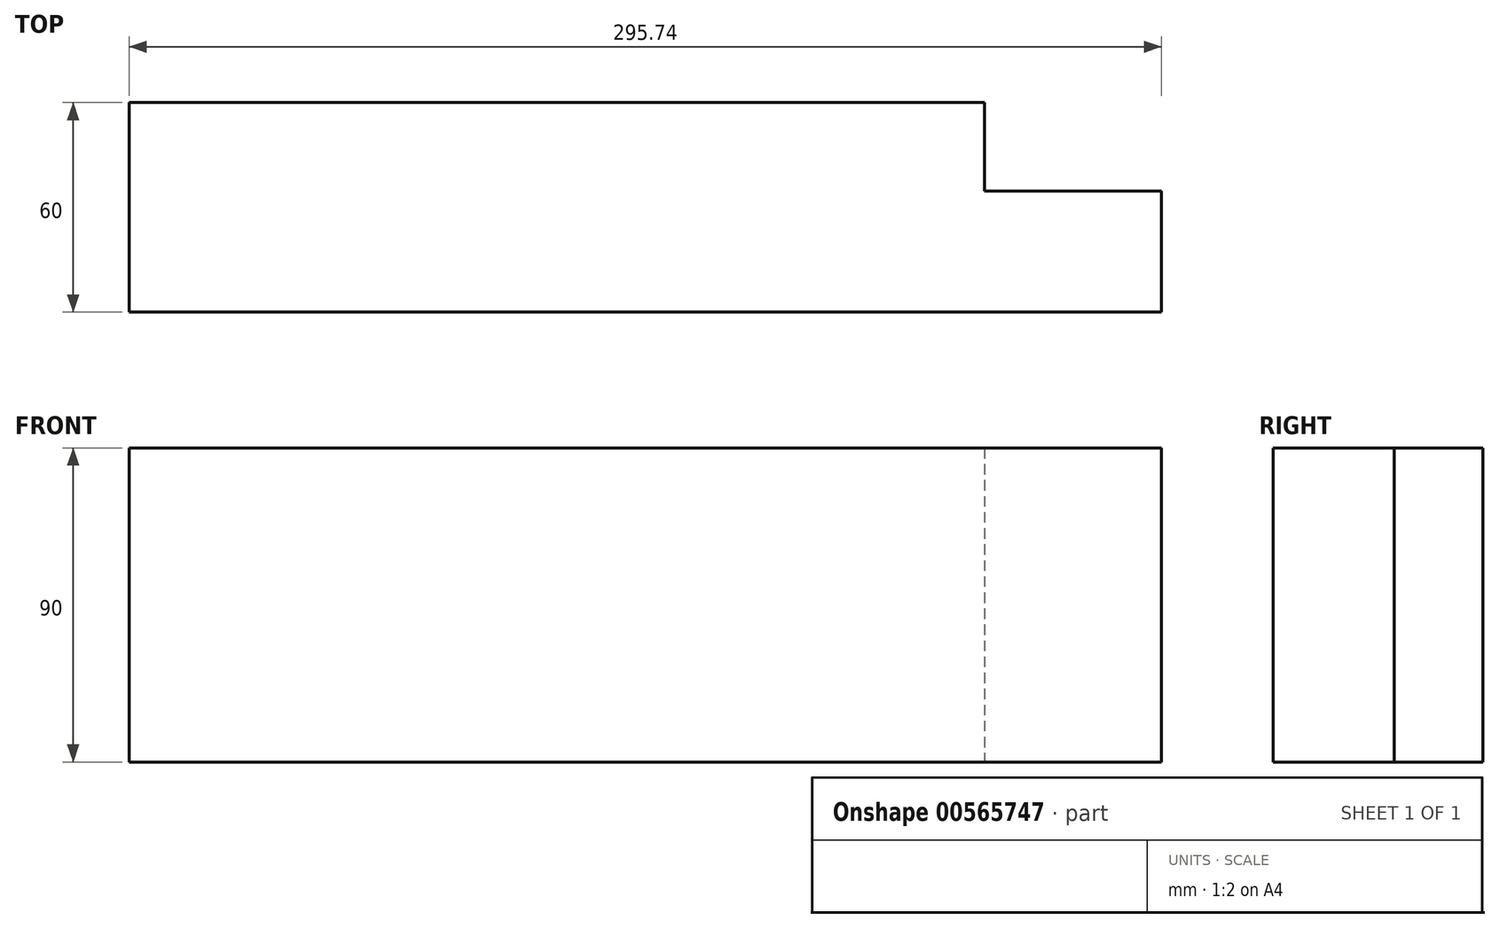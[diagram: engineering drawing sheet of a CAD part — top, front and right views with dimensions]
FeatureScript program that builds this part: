
annotation { "Feature Type Name" : "Feature", "Feature Type Description" : "" }
export const myFeature = defineFeature(function(context is Context, id is Id, definition is map)
    precondition{}
    {
        {
            var Q0;
            Q0=qCreatedBy(makeId("Top.planeOp"),FACE);
            var sketch = newSketch(context, id + "F0", { "sketchPlane" : qUnion([Q0])});
            skLineSegment(sketch, "E0.bottom", {"start": v(75.6, 30) * mm, "end": v(-220.15, 30) * mm});
            skLineSegment(sketch, "E0.top", {"start": v(220.15, -30) * mm, "end": v(-75.6, -30) * mm});
            skPoint(sketch, "E0.middle", {"position": v(0, 0) * mm});
            skLineSegment(sketch, "E1", {"start": v(75.6, 30) * mm, "end": v(169.42, 30) * mm});
            skLineSegment(sketch, "E2", {"start": v(169.42, 30) * mm, "end": v(169.42, 4.64) * mm});
            skLineSegment(sketch, "E3", {"start": v(169.42, 4.64) * mm, "end": v(220.15, 4.64) * mm});
            skLineSegment(sketch, "E4", {"start": v(220.15, 4.64) * mm, "end": v(220.15, -30) * mm});
            skLineSegment(sketch, "E5", {"start": v(-75.6, -30) * mm, "end": v(-75.6, 30) * mm});
            skSolve(sketch);
        }
        {
            var Q0;
            Q0 = qSketchRegion(id + "F0", true);
            extrude(context, id + "F1", {"entities" : qUnion([Q0]), "depth" : 90 * mm, "offsetDistance" : 25 * mm});
        }
    });
